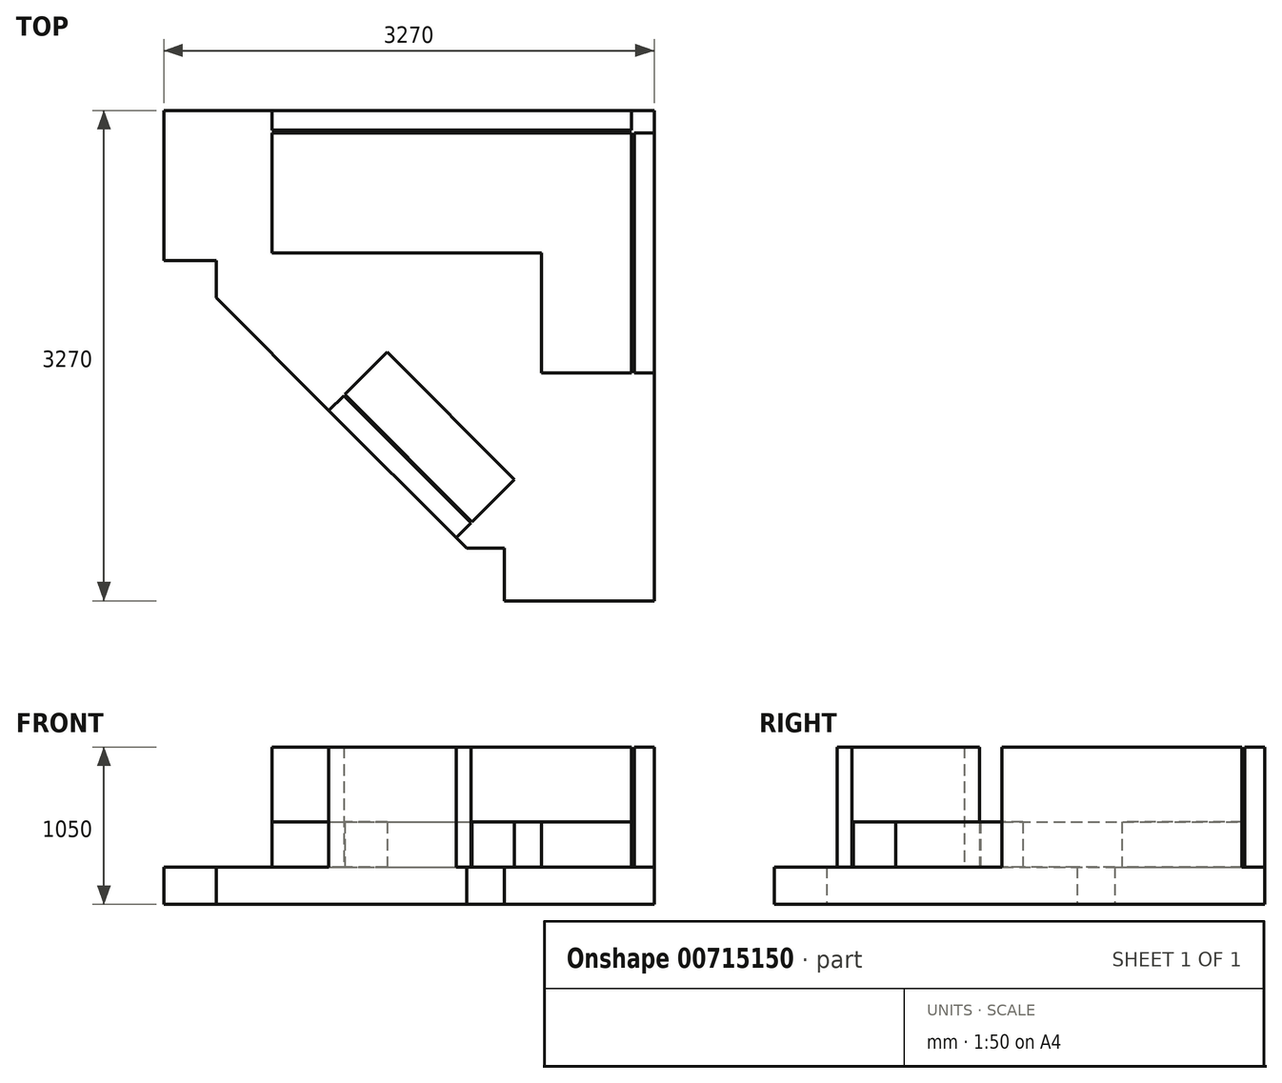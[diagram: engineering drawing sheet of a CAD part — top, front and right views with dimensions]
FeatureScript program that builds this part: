
annotation { "Feature Type Name" : "Feature", "Feature Type Description" : "" }
export const myFeature = defineFeature(function(context is Context, id is Id, definition is map)
    precondition{}
    {
        {
            var Q0;
            Q0=qCreatedBy(makeId("Top.planeOp"),FACE);
            var sketch = newSketch(context, id + "F0", { "sketchPlane" : qUnion([Q0])});
            skLineSegment(sketch, "E0", {"start": v(0, 0) * mm, "end": v(-3270, 0) * mm});
            skLineSegment(sketch, "E1", {"start": v(0, 0) * mm, "end": v(0, -3270) * mm});
            skLineSegment(sketch, "E2", {"start": v(0, -3270) * mm, "end": v(-1000, -3270) * mm});
            skLineSegment(sketch, "E3", {"start": v(-1000, -3270) * mm, "end": v(-1000, -2920) * mm});
            skLineSegment(sketch, "E4", {"start": v(-2920, -1000) * mm, "end": v(-3270, -1000) * mm});
            skLineSegment(sketch, "E5", {"start": v(-3270, -1000) * mm, "end": v(-3270, 0) * mm});
            skLineSegment(sketch, "E6", {"start": v(-2920, -1000) * mm, "end": v(-2920, -1250) * mm});
            skLineSegment(sketch, "E7", {"start": v(-2920, -1250) * mm, "end": v(-1250, -2920) * mm});
            skLineSegment(sketch, "E8", {"start": v(-1250, -2920) * mm, "end": v(-1000, -2920) * mm});
            skSolve(sketch);
        }
        {
            var Q0;
            Q0 = qSketchRegion(id + "F0", true);
            extrude(context, id + "F1", {"entities" : qUnion([Q0]), "depth" : 250 * mm, "offsetDistance" : 25 * mm});
        }
        {
            var Q0;
            Q0=makeQuery(id+"F1.opExtrude","CAP_FACE",FACE,{"disambiguationData":[OSD([sQuery(id+"F0.wireOp",EDGE,"E0"),sQuery(id+"F0.wireOp",EDGE,"E1"),sQuery(id+"F0.wireOp",EDGE,"E2"),sQuery(id+"F0.wireOp",EDGE,"E3"),sQuery(id+"F0.wireOp",EDGE,"E4"),sQuery(id+"F0.wireOp",EDGE,"E5"),sQuery(id+"F0.wireOp",EDGE,"E6"),sQuery(id+"F0.wireOp",EDGE,"E7"),sQuery(id+"F0.wireOp",EDGE,"E8")])],"isStart":false});
            var sketch = newSketch(context, id + "F2", { "sketchPlane" : qUnion([Q0])});
            skLineSegment(sketch, "E9", {"start": v(-2920, -1250) * mm, "end": v(-2002.59, -1003.3) * mm});
            skLineSegment(sketch, "E10.bottom", {"start": v(-1780.33, -1611.85) * mm, "end": v(-931.8, -2460.38) * mm});
            skLineSegment(sketch, "E10.top", {"start": v(-2063.17, -1894.7) * mm, "end": v(-1214.64, -2743.22) * mm});
            skLineSegment(sketch, "E10.left", {"start": v(-1780.33, -1611.85) * mm, "end": v(-2063.17, -1894.7) * mm});
            skLineSegment(sketch, "E10.right", {"start": v(-931.8, -2460.38) * mm, "end": v(-1214.64, -2743.22) * mm});
            skLineSegment(sketch, "E11.bottom", {"start": v(-150, -1750) * mm, "end": v(-750, -1750) * mm});
            skLineSegment(sketch, "E11.top", {"start": v(-150, -950) * mm, "end": v(-750, -950) * mm});
            skLineSegment(sketch, "E11.left", {"start": v(-150, -1750) * mm, "end": v(-150, -950) * mm});
            skLineSegment(sketch, "E11.right", {"start": v(-750, -1750) * mm, "end": v(-750, -950) * mm});
            skLineSegment(sketch, "E12.bottom", {"start": v(-2550, -150) * mm, "end": v(-150, -150) * mm});
            skLineSegment(sketch, "E12.top", {"start": v(-2550, -950) * mm, "end": v(-150, -950) * mm});
            skLineSegment(sketch, "E12.left", {"start": v(-2550, -150) * mm, "end": v(-2550, -950) * mm});
            skLineSegment(sketch, "E12.right", {"start": v(-150, -150) * mm, "end": v(-150, -950) * mm});
            skSolve(sketch);
        }
        {
            var Q0;
            Q0 = qSketchRegion(id + "F2", true);
            extrude(context, id + "F3", {"entities" : qUnion([Q0]), "operationType" : NewBodyOperationType.ADD, "depth" : 300 * mm, "offsetDistance" : 25 * mm});
        }
        {
            var Q0;
            Q0=makeQuery(id+"F1.opExtrude","CAP_FACE",FACE,{"disambiguationData":[OSD([sQuery(id+"F0.wireOp",EDGE,"E0"),sQuery(id+"F0.wireOp",EDGE,"E1"),sQuery(id+"F0.wireOp",EDGE,"E2"),sQuery(id+"F0.wireOp",EDGE,"E3"),sQuery(id+"F0.wireOp",EDGE,"E4"),sQuery(id+"F0.wireOp",EDGE,"E5"),sQuery(id+"F0.wireOp",EDGE,"E6"),sQuery(id+"F0.wireOp",EDGE,"E7"),sQuery(id+"F0.wireOp",EDGE,"E8")])],"isStart":false});
            var sketch = newSketch(context, id + "F4", { "sketchPlane" : qUnion([Q0])});
            skLineSegment(sketch, "E13.top", {"start": v(-2550, 0) * mm, "end": v(-150, 0) * mm});
            skLineSegment(sketch, "E13.left", {"start": v(-2550, -130.9) * mm, "end": v(-2550, 0) * mm});
            skLineSegment(sketch, "E13.right", {"start": v(-150, -130.9) * mm, "end": v(-150, 0) * mm});
            skLineSegment(sketch, "E14.bottom", {"start": v(-130.97, -1750) * mm, "end": v(0, -1750) * mm});
            skLineSegment(sketch, "E14.top", {"start": v(-130.97, -150) * mm, "end": v(0, -150) * mm});
            skLineSegment(sketch, "E14.right", {"start": v(0, -1750) * mm, "end": v(0, -150) * mm});
            skLineSegment(sketch, "E15", {"start": v(-2070.24, -1901.77) * mm, "end": v(-2169.24, -2000.76) * mm});
            skLineSegment(sketch, "E16", {"start": v(-1221.72, -2750.3) * mm, "end": v(-1320.71, -2849.29) * mm});
            skLineSegment(sketch, "E17", {"start": v(-1320.71, -2849.29) * mm, "end": v(-2169.24, -2000.76) * mm});
            skLineSegment(sketch, "E18", {"start": v(-2070.24, -1901.77) * mm, "end": v(-1221.72, -2750.3) * mm});
            skLineSegment(sketch, "E19", {"start": v(-2550, -130.9) * mm, "end": v(-150, -130.9) * mm});
            skLineSegment(sketch, "E20", {"start": v(-130.97, -150) * mm, "end": v(-130.97, -1750) * mm});
            skPoint(sketch, "E13.bottom.end.orphan", {"position": v(-150, -150) * mm});
            skSolve(sketch);
        }
        {
            var Q0;
            Q0 = qSketchRegion(id + "F4", true);
            extrude(context, id + "F5", {"entities" : qUnion([Q0]), "operationType" : NewBodyOperationType.ADD, "depth" : 800 * mm, "offsetDistance" : 25 * mm});
        }
        {
            var Q0;
            Q0 = qSketchRegion(id + "F4", true);
            extrude(context, id + "F6", {"entities" : qUnion([Q0]), "operationType" : NewBodyOperationType.ADD, "depth" : 800 * mm, "offsetDistance" : 25 * mm});
        }
    });
